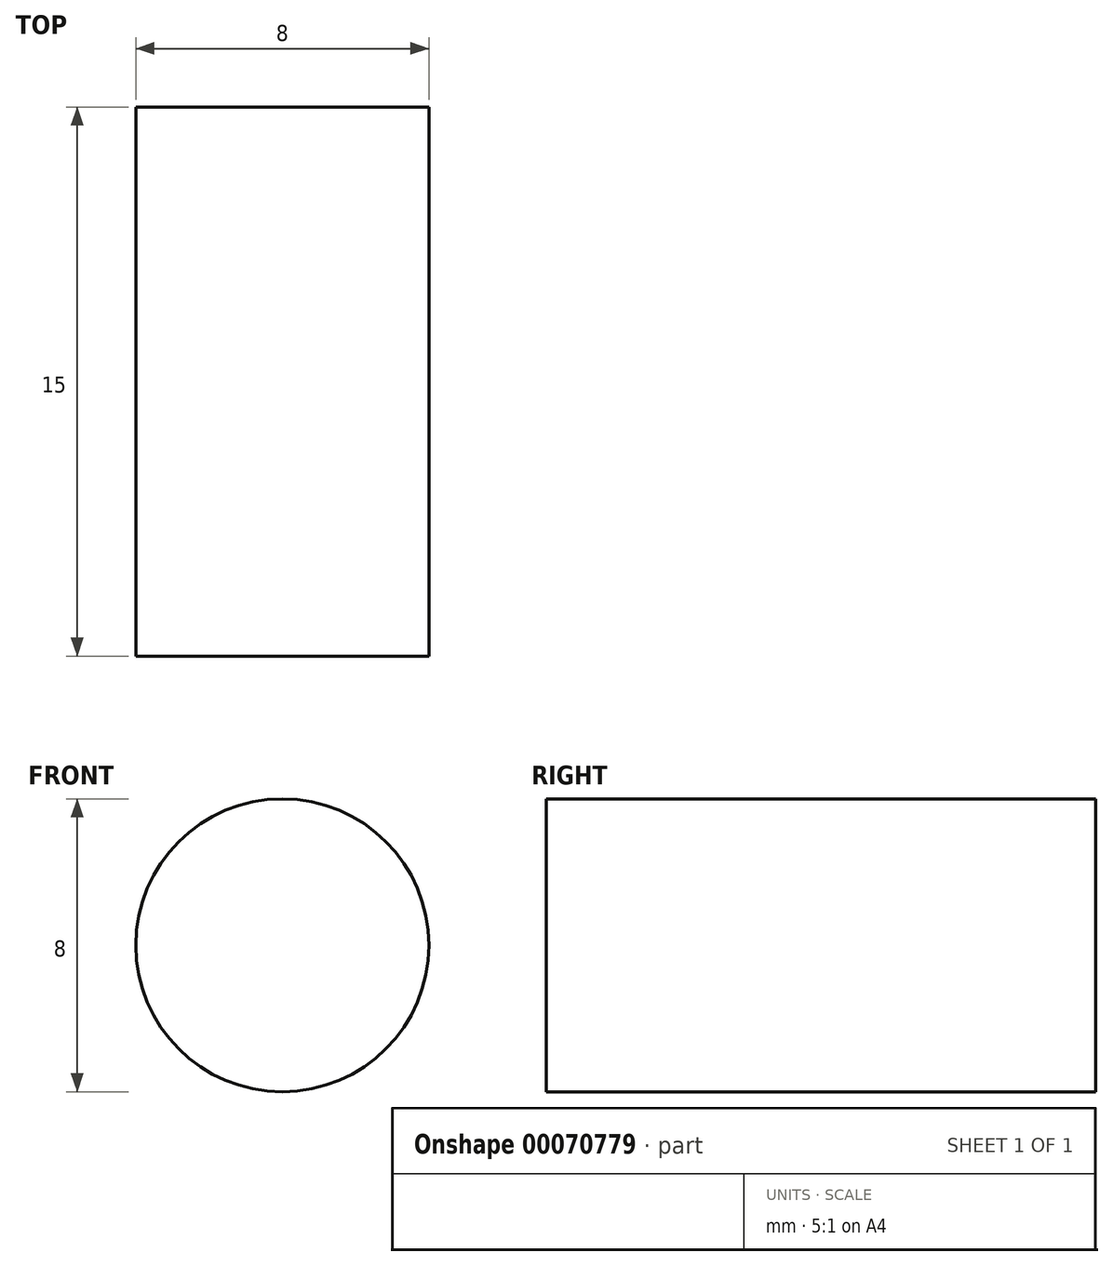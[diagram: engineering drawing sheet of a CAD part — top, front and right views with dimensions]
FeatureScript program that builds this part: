
annotation { "Feature Type Name" : "Feature", "Feature Type Description" : "" }
export const myFeature = defineFeature(function(context is Context, id is Id, definition is map)
    precondition{}
    {
        {
            var Q0;
            Q0=qCreatedBy(makeId("Front.planeOp"),FACE);
            var sketch = newSketch(context, id + "F0", { "sketchPlane" : qUnion([Q0])});
            skCircle(sketch, "E0", {"center": v(0, 0) * mm, "radius": 4 * mm});
            skSolve(sketch);
        }
        {
            var Q0;
            Q0 = qSketchRegion(id + "F0", true);
            extrude(context, id + "F1", {"entities" : qUnion([Q0]), "depth" : 15 * mm});
        }
    });
